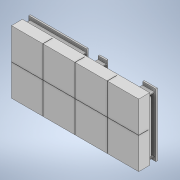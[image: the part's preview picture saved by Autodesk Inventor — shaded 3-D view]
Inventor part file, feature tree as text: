
AUTODESK INVENTOR PART (.ipt)
format: ipt  version: 2021 (Build 250183000, 183)  size: 350,208 bytes
history: native  units: mm
features: sketch x14, extrude x12, hole x1
ambient origin geometry x8: Origin, YZ Plane, XZ Plane, XY Plane, X Axis, Y Axis, Z Axis, Center Point
bodies: Solid1 (feature_tree)
feature tree (27):
  extrude  "Extrusion1"  Depth=40.0mm
  extrude  "Extrusion2"  Depth=20.0mm
  extrude  "Extrusion3"  Depth=19.9mm
  extrude  "Extrusion4"  Depth=6.0mm TaperAngle=0.0deg
  extrude  "Extrusion5"  Depth=0.2mm
  extrude  "Extrusion6"  Depth=19.9mm
  hole  "Hole1"  [1 undecoded]
  extrude  "Extrusion8"  Depth=6.0mm TaperAngle=0.0deg
  sketch  "Sketch10"  dims[d19=0.5mm d20=2.0mm]
  extrude  "Extrusion9"  Depth=2.0mm
  extrude  "Extrusion10"  Depth=0.5mm
  extrude  "Extrusion11"  Depth=1.0mm
  extrude  "Extrusion12"  Depth=1.0mm TaperAngle=0.0deg
  extrude  "Extrusion13"  Depth=7.5mm
  sketch  "Sketch1"  dims[d0=81.0mm d1=40.0mm]
  sketch  "Sketch2"  dims[d2=20.0mm d3=40.5mm]
  sketch  "Sketch3"  dims[d4=7.0mm d5=0.0mm d6=19.9mm]
  sketch  "Sketch4"  dims[d7=19.9mm d8=6.0mm d9=0.0mm]
  sketch  "Sketch5"  dims[d10=0.2mm d11=0.2mm]
  sketch  "Sketch6"  dims[d12=0.2mm d13=19.9mm]
  sketch  "Sketch8"  dims[d14=19.9mm d15=40.4mm]
  sketch  "Sketch9"  dims[d16=40.4mm d17=6.0mm d18=0.0mm]
  sketch  "Sketch11"  dims[d21=2.0mm d22=0.5mm]
  sketch  "Sketch12"  dims[d23=1.0mm d24=1.0mm]
  sketch  "Sketch13"  dims[d25=5.0mm d26=0.0mm d27=1.0mm d28=0.0mm]
  sketch  "Sketch14"  dims[d29=7.5mm d30=3.75mm]
  sketch  "Sketch15"  dims[d31=18.0mm d32=1.0mm d33=0.0mm d39=5.0mm d40=35.0mm d41=5.0mm d42=5.0mm d43=40.5mm d44=5.0mm d45=5.0mm d46=76.03mm d47=76.03mm d48=35.0mm d49=23.0mm d50=23.0mm d51=37.0mm d52=37.0mm d53=34.0mm d54=34.0mm d55=47.0mm d56=47.0mm d57=2.0mm d58=6.0mm d59=4.0mm d60=2.0mm d61=90.0deg d62=1.0mm d63=20.594885mm d64=0.5mm d65=5.0mm d66=0.0mm d67=4.2mm d68=13.0mm d69=3.0mm d70=4.2mm d71=13.0mm d72=3.0mm d73=1.0mm d74=0.0mm d75=5.2mm d76=12.44mm d77=23.1mm d78=4.5mm d79=0.0mm d80=1.0mm d81=1.0mm d82=1.0mm d83=3.0mm d84=2.0mm d85=0.0mm d86=22.4mm d87=37.6mm d88=43.0mm d89=58.3mm d90=2.7mm d91=6.2mm d92=0.3mm d93=0.3mm d94=0.3mm d95=0.3mm d96=0.3mm d97=0.3mm d98=7.0mm d99=0.0mm d100=1.0mm d101=1.0mm d102=1.0mm d103=1.0mm d104=1.0mm d105=1.0mm d106=1.0mm d107=1.0mm d108=5.0mm d109=3.0mm d110=0.0mm]
note: 1 required parameter value undecoded (feature->parameter linkage not recoverable at this tier; creation-order binding heuristic only, values carry confidence <= 0.55)
